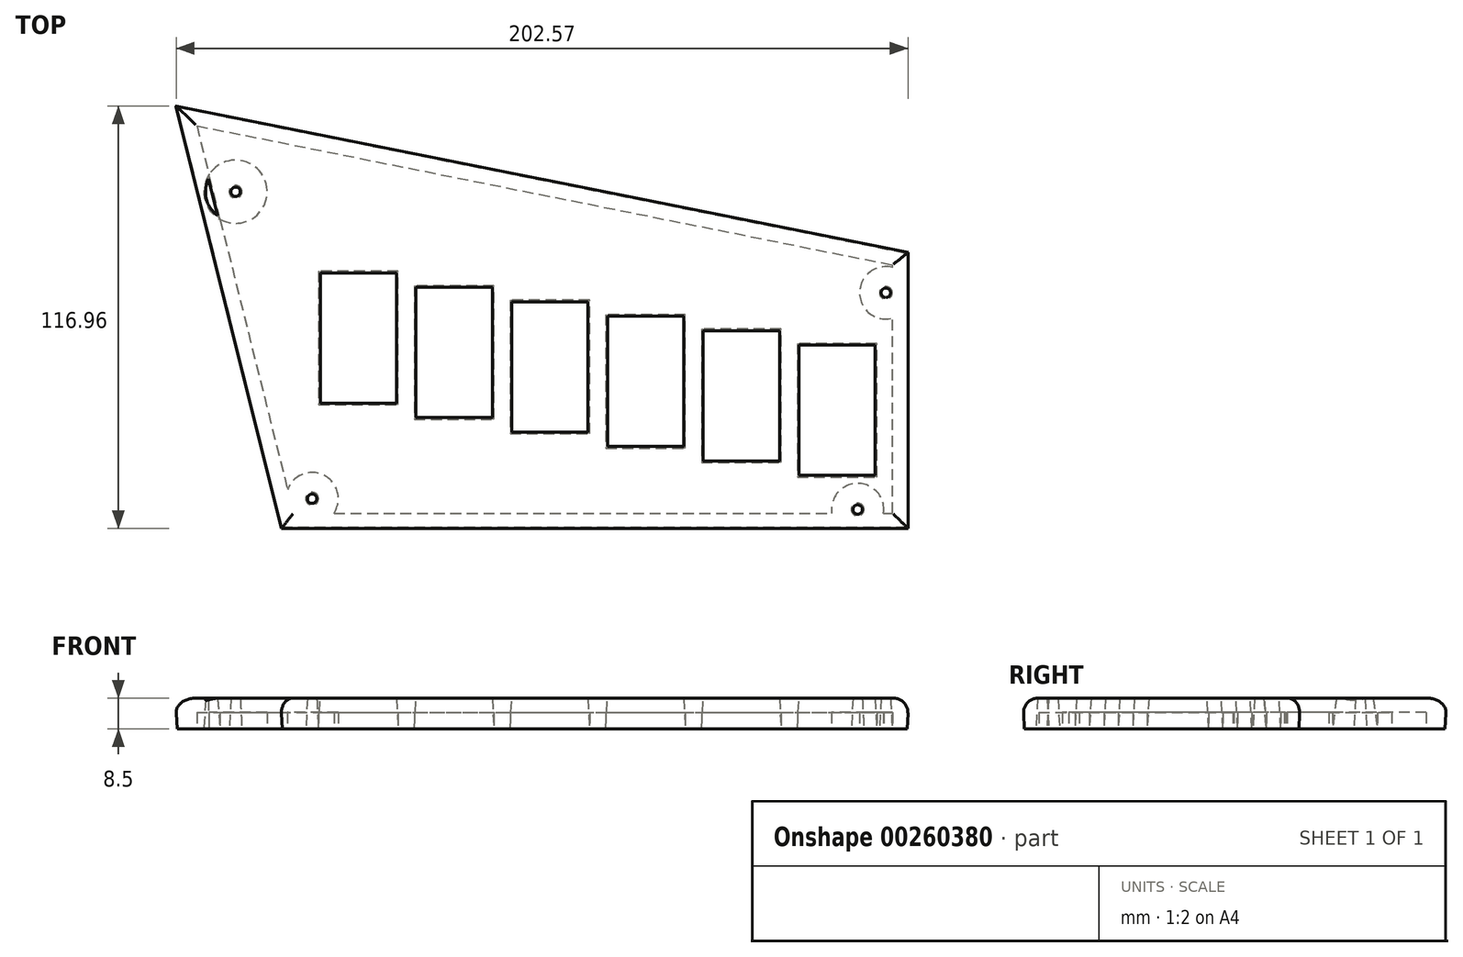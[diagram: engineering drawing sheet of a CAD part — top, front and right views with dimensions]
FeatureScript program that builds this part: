
annotation { "Feature Type Name" : "Feature", "Feature Type Description" : "" }
export const myFeature = defineFeature(function(context is Context, id is Id, definition is map)
    precondition{}
    {
        {
            var Q0;
            Q0=qCreatedBy(makeId("Top.planeOp"),FACE);
            var sketch = newSketch(context, id + "F0", { "sketchPlane" : qUnion([Q0])});
            skPoint(sketch, "E0.middle", {"position": v(0, 0) * mm});
            skCircle(sketch, "E1", {"center": v(-100.12, 36.19) * mm, "radius": 1.75 * mm});
            skCircle(sketch, "E2", {"center": v(-78.93, -48.81) * mm, "radius": 1.75 * mm});
            skCircle(sketch, "E3", {"center": v(72.07, -51.81) * mm, "radius": 1.75 * mm});
            skCircle(sketch, "E4", {"center": v(79.88, 8.19) * mm, "radius": 1.75 * mm});
            skLineSegment(sketch, "E5", {"start": v(-116.27, 59.62) * mm, "end": v(-87.24, -56.81) * mm});
            skLineSegment(sketch, "E6.bottom", {"start": v(-77.12, 14.19) * mm, "end": v(-55.12, 14.19) * mm});
            skLineSegment(sketch, "E6.top", {"start": v(-77.12, -22.81) * mm, "end": v(-55.12, -22.81) * mm});
            skLineSegment(sketch, "E6.left", {"start": v(-77.12, 14.19) * mm, "end": v(-77.12, -22.81) * mm});
            skLineSegment(sketch, "E6.right", {"start": v(-55.12, 14.19) * mm, "end": v(-55.12, -22.81) * mm});
            skLineSegment(sketch, "E7.bottom", {"start": v(-50.62, 10.19) * mm, "end": v(-28.62, 10.19) * mm});
            skLineSegment(sketch, "E7.top", {"start": v(-50.62, -26.81) * mm, "end": v(-28.62, -26.81) * mm});
            skLineSegment(sketch, "E7.left", {"start": v(-50.62, 10.19) * mm, "end": v(-50.62, -26.81) * mm});
            skLineSegment(sketch, "E7.right", {"start": v(-28.62, 10.19) * mm, "end": v(-28.62, -26.81) * mm});
            skLineSegment(sketch, "E8", {"start": v(-87.24, -56.81) * mm, "end": v(85.76, -56.81) * mm});
            skLineSegment(sketch, "E9", {"start": v(85.76, -56.81) * mm, "end": v(85.76, 19.19) * mm});
            skLineSegment(sketch, "E10", {"start": v(-116.27, 59.62) * mm, "end": v(85.76, 19.19) * mm});
            skLineSegment(sketch, "E11.bottom", {"start": v(-24.12, 6.19) * mm, "end": v(-2.12, 6.19) * mm});
            skLineSegment(sketch, "E11.top", {"start": v(-24.12, -30.81) * mm, "end": v(-2.12, -30.81) * mm});
            skLineSegment(sketch, "E11.left", {"start": v(-24.12, 6.19) * mm, "end": v(-24.12, -30.81) * mm});
            skLineSegment(sketch, "E11.right", {"start": v(-2.12, 6.19) * mm, "end": v(-2.12, -30.81) * mm});
            skLineSegment(sketch, "E12.bottom", {"start": v(2.38, 2.19) * mm, "end": v(24.38, 2.19) * mm});
            skLineSegment(sketch, "E12.top", {"start": v(2.38, -34.81) * mm, "end": v(24.38, -34.81) * mm});
            skLineSegment(sketch, "E12.left", {"start": v(2.38, 2.19) * mm, "end": v(2.38, -34.81) * mm});
            skLineSegment(sketch, "E12.right", {"start": v(24.38, 2.19) * mm, "end": v(24.38, -34.81) * mm});
            skLineSegment(sketch, "E13.bottom", {"start": v(28.88, -1.81) * mm, "end": v(50.88, -1.81) * mm});
            skLineSegment(sketch, "E13.top", {"start": v(28.88, -38.81) * mm, "end": v(50.88, -38.81) * mm});
            skLineSegment(sketch, "E13.left", {"start": v(28.88, -1.81) * mm, "end": v(28.88, -38.81) * mm});
            skLineSegment(sketch, "E13.right", {"start": v(50.88, -1.81) * mm, "end": v(50.88, -38.81) * mm});
            skLineSegment(sketch, "E14.bottom", {"start": v(55.38, -5.81) * mm, "end": v(77.38, -5.81) * mm});
            skLineSegment(sketch, "E14.top", {"start": v(55.38, -42.81) * mm, "end": v(77.38, -42.81) * mm});
            skLineSegment(sketch, "E14.left", {"start": v(55.38, -5.81) * mm, "end": v(55.38, -42.81) * mm});
            skLineSegment(sketch, "E14.right", {"start": v(77.38, -5.81) * mm, "end": v(77.38, -42.81) * mm});
            skLineSegment(sketch, "E15.0", {"start": v(-84.12, -52.81) * mm, "end": v(81.76, -52.81) * mm});
            skLineSegment(sketch, "E15.1", {"start": v(-110.86, 54.46) * mm, "end": v(-84.12, -52.81) * mm});
            skLineSegment(sketch, "E15.2", {"start": v(-110.86, 54.46) * mm, "end": v(81.76, 15.9) * mm});
            skLineSegment(sketch, "E15.3", {"start": v(81.76, -52.81) * mm, "end": v(81.76, 15.9) * mm});
            skCircle(sketch, "E16.0", {"center": v(-100.12, 36.19) * mm, "radius": 8.75 * mm});
            skCircle(sketch, "E17.0", {"center": v(-78.93, -48.81) * mm, "radius": 7.25 * mm});
            skCircle(sketch, "E18.0", {"center": v(79.88, 8.19) * mm, "radius": 7.25 * mm});
            skCircle(sketch, "E19.0", {"center": v(72.07, -51.81) * mm, "radius": 7.25 * mm});
            skSolve(sketch);
        }
        {
            var Q0;
            {var subQ0=sQuery(id+"F0.wireOp",EDGE,"E15.1");var subQ1=sQuery(id+"F0.wireOp",EDGE,"E15.0");var subQ2=makeQuery(id+"F0.imprint","INTERSECT",VERTEX,{"derivedFrom":[subQ1,subQ0]});Q0=makeQuery(id+"F0.imprint","IMPRINT",FACE,{"disambiguationData":[TD([[makeQuery(id+"F0.imprint","IMPRINT",EDGE,{"disambiguationData":[TD([[subQ2,-1.0]])],"derivedFrom":subQ1}),-1.0]])]});}
            var Q1;
            Q1=makeQuery(id+"F0.imprint","IMPRINT",FACE,{"disambiguationData":[TD([[makeQuery(id+"F0.imprint","IMPRINT",EDGE,{"derivedFrom":sQuery(id+"F0.wireOp",EDGE,"E2")}),-1.0]])]});
            var Q2;
            {var subQ0=sQuery(id+"F0.wireOp",EDGE,"E15.0");var subQ1=sQuery(id+"F0.wireOp",EDGE,"E3");var subQ8=makeQuery(id+"F0.imprint","INTERSECT",VERTEX,{"disambiguationData":[OD(0.0)],"derivedFrom":[subQ1,subQ0]});Q2=makeQuery(id+"F0.imprint","IMPRINT",FACE,{"disambiguationData":[TD([[makeQuery(id+"F0.imprint","IMPRINT",EDGE,{"disambiguationData":[TD([[subQ8,-1.0]])],"derivedFrom":subQ1}),-1.0]])]});}
            var Q3;
            {var subQ0=sQuery(id+"F0.wireOp",EDGE,"E15.0");var subQ1=sQuery(id+"F0.wireOp",EDGE,"E3");var subQ2=makeQuery(id+"F0.imprint","INTERSECT",VERTEX,{"disambiguationData":[OD(0.0)],"derivedFrom":[subQ1,subQ0]});Q3=makeQuery(id+"F0.imprint","IMPRINT",FACE,{"disambiguationData":[TD([[makeQuery(id+"F0.imprint","IMPRINT",EDGE,{"disambiguationData":[TD([[subQ2,1.0]])],"derivedFrom":subQ1}),-1.0]])]});}
            var Q4;
            Q4=makeQuery(id+"F0.imprint","IMPRINT",FACE,{"disambiguationData":[TD([[makeQuery(id+"F0.imprint","IMPRINT",EDGE,{"derivedFrom":sQuery(id+"F0.wireOp",EDGE,"E4")}),-1.0]])]});
            var Q5;
            {var subQ0=sQuery(id+"F0.wireOp",EDGE,"E18.0");var subQ1=sQuery(id+"F0.wireOp",EDGE,"E9");var subQ2=makeQuery(id+"F0.imprint","INTERSECT",VERTEX,{"disambiguationData":[OD(0.0)],"derivedFrom":[subQ1,subQ0]});Q5=makeQuery(id+"F0.imprint","IMPRINT",FACE,{"disambiguationData":[TD([[makeQuery(id+"F0.imprint","IMPRINT",EDGE,{"disambiguationData":[TD([[subQ2,-1.0]])],"derivedFrom":subQ1}),1.0]])]});}
            var Q6;
            Q6=makeQuery(id+"F0.imprint","IMPRINT",FACE,{"disambiguationData":[TD([[makeQuery(id+"F0.imprint","IMPRINT",EDGE,{"derivedFrom":sQuery(id+"F0.wireOp",EDGE,"E1")}),-1.0]])]});
            var Q7;
            {var subQ0=sQuery(id+"F0.wireOp",EDGE,"E16.0");var subQ1=sQuery(id+"F0.wireOp",EDGE,"E15.1");var subQ2=makeQuery(id+"F0.imprint","INTERSECT",VERTEX,{"disambiguationData":[OD(0.0)],"derivedFrom":[subQ1,subQ0]});Q7=makeQuery(id+"F0.imprint","IMPRINT",FACE,{"disambiguationData":[TD([[makeQuery(id+"F0.imprint","IMPRINT",EDGE,{"disambiguationData":[TD([[subQ2,-1.0]])],"derivedFrom":subQ1}),-1.0]])]});}
            var Q8;
            {var subQ12=sQuery(id+"F0.wireOp",EDGE,"E5");Q8=makeQuery(id+"F0.imprint","IMPRINT",FACE,{"disambiguationData":[TD([[makeQuery(id+"F0.imprint","IMPRINT",EDGE,{"derivedFrom":subQ12}),1.0]])]});}
            var Q9;
            {var subQ7=sQuery(id+"F0.wireOp",EDGE,"E9");var subQ8=sQuery(id+"F0.wireOp",EDGE,"E8");var subQ9=makeQuery(id+"F0.imprint","INTERSECT",VERTEX,{"derivedFrom":[subQ8,subQ7]});Q9=makeQuery(id+"F0.imprint","IMPRINT",FACE,{"disambiguationData":[TD([[makeQuery(id+"F0.imprint","IMPRINT",EDGE,{"disambiguationData":[TD([[subQ9,1.0]])],"derivedFrom":subQ8}),1.0]])]});}
            var Q10;
            Q10=makeQuery(id+"F0.imprint","IMPRINT",FACE,{"disambiguationData":[TD([[makeQuery(id+"F0.imprint","IMPRINT",EDGE,{"derivedFrom":sQuery(id+"F0.wireOp",EDGE,"E6.bottom")}),1.0]])]});
            extrude(context, id + "F1", {"entities" : qUnion([Q0, Q1, Q2, Q3, Q4, Q5, Q6, Q7, Q8, Q9, Q10]), "depth" : 8.5 * mm, "hasDraft" : true, "draftAngle" : 3 * degree});
        }
        {
            var Q0;
            Q0=makeQuery(id+"F0.imprint","IMPRINT",FACE,{"disambiguationData":[TD([[makeQuery(id+"F0.imprint","IMPRINT",EDGE,{"derivedFrom":sQuery(id+"F0.wireOp",EDGE,"E6.bottom")}),1.0]])]});
            extrude(context, id + "F2", {"entities" : qUnion([Q0]), "operationType" : NewBodyOperationType.REMOVE, "depth" : 4.5 * mm});
        }
        {
            var Q0;
            Q0=makeQuery(id+"F1.opExtrude","CAP_EDGE",EDGE,{"disambiguationData":[OSD([sQuery(id+"F0.wireOp",EDGE,"E5")])],"isStart":false});
            var Q1;
            Q1=makeQuery(id+"F1.opExtrude","CAP_EDGE",EDGE,{"disambiguationData":[OSD([sQuery(id+"F0.wireOp",EDGE,"E10")])],"isStart":false});
            var Q2;
            Q2=makeQuery(id+"F1.opExtrude","CAP_EDGE",EDGE,{"disambiguationData":[OSD([sQuery(id+"F0.wireOp",EDGE,"E8")])],"isStart":false});
            var Q3;
            Q3=makeQuery(id+"F1.opExtrude","CAP_EDGE",EDGE,{"disambiguationData":[OSD([sQuery(id+"F0.wireOp",EDGE,"E9")])],"isStart":false});
            fillet(context, id + "F3", {"entities" : qUnion([Q0, Q1, Q2, Q3]), "radius" : 4 * mm, "tangentPropagation" : true, "allowEdgeOverflow" : false});
        }
    });
